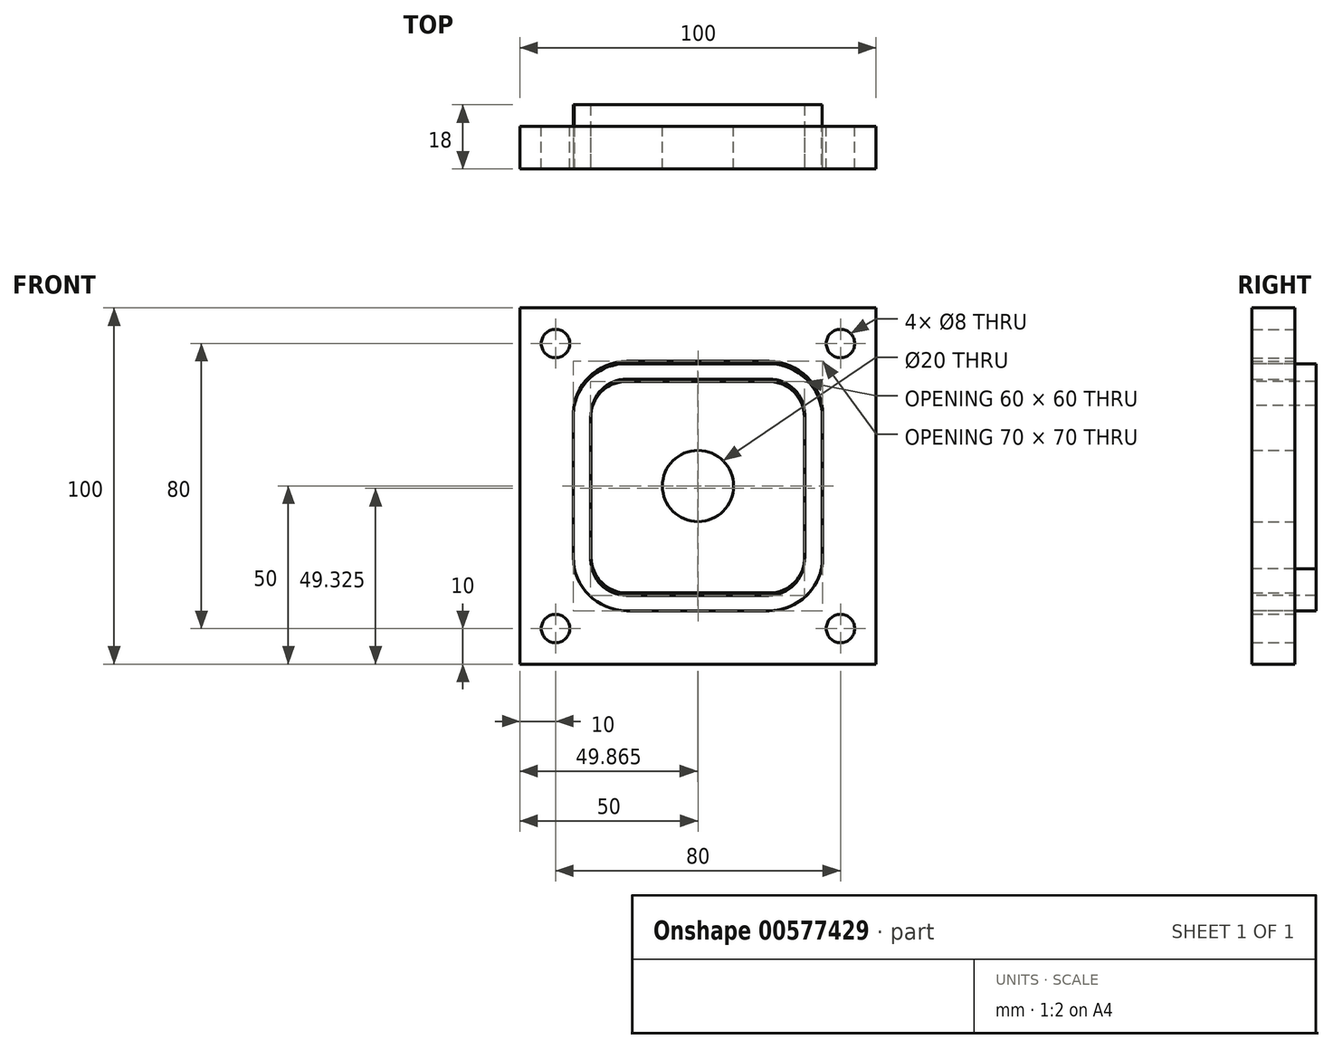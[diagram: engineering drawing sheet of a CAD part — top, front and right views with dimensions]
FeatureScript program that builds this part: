
annotation { "Feature Type Name" : "Feature", "Feature Type Description" : "" }
export const myFeature = defineFeature(function(context is Context, id is Id, definition is map)
    precondition{}
    {
        {
            var Q0;
            Q0=qCreatedBy(makeId("Front.planeOp"),FACE);
            var sketch = newSketch(context, id + "F0", { "sketchPlane" : qUnion([Q0])});
            skLineSegment(sketch, "E0", {"start": v(50, -50) * mm, "end": v(50, 50) * mm});
            skLineSegment(sketch, "E1", {"start": v(50, 50) * mm, "end": v(-50, 50) * mm});
            skLineSegment(sketch, "E2", {"start": v(-50, 50) * mm, "end": v(-50, -50) * mm});
            skLineSegment(sketch, "E3", {"start": v(-50, -50) * mm, "end": v(50, -50) * mm});
            skCircle(sketch, "E4", {"center": v(40, -40) * mm, "radius": 4 * mm});
            skCircle(sketch, "E5", {"center": v(40, 40) * mm, "radius": 4 * mm});
            skCircle(sketch, "E6", {"center": v(-40, -40) * mm, "radius": 4 * mm});
            skCircle(sketch, "E7", {"center": v(-40, 40) * mm, "radius": 4 * mm});
            skCircle(sketch, "E8", {"center": v(0, 0) * mm, "radius": 10 * mm});
            skLineSegment(sketch, "E9", {"start": v(35, -20) * mm, "end": v(35, 20) * mm});
            skLineSegment(sketch, "E10", {"start": v(20, 35) * mm, "end": v(-20, 35) * mm});
            skLineSegment(sketch, "E11", {"start": v(-35, 20) * mm, "end": v(-35, -20) * mm});
            skLineSegment(sketch, "E12", {"start": v(20, -35) * mm, "end": v(-20, -35) * mm});
            skArc(sketch, "E13", {"start": v(-35, -20) * mm, "mid": v(-30.6, -30.6) * mm, "end": v(-20, -35) * mm});
            skArc(sketch, "E14", {"start": v(20, -35) * mm, "mid": v(30.6, -30.6) * mm, "end": v(35, -20) * mm});
            skArc(sketch, "E15", {"start": v(35, 20) * mm, "mid": v(30.6, 30.6) * mm, "end": v(20, 35) * mm});
            skArc(sketch, "E16", {"start": v(-20, 35) * mm, "mid": v(-30.6, 30.6) * mm, "end": v(-35, 20) * mm});
            skLineSegment(sketch, "E17", {"start": v(20, -30) * mm, "end": v(-20, -30) * mm});
            skLineSegment(sketch, "E18", {"start": v(-30, -20) * mm, "end": v(-30, 20) * mm});
            skLineSegment(sketch, "E19", {"start": v(-20, 30) * mm, "end": v(20, 30) * mm});
            skLineSegment(sketch, "E20", {"start": v(30, -20) * mm, "end": v(30, 20) * mm});
            skArc(sketch, "E21", {"start": v(20, -30) * mm, "mid": v(27.07, -27.07) * mm, "end": v(30, -20) * mm});
            skArc(sketch, "E22", {"start": v(30, 20) * mm, "mid": v(27.07, 27.07) * mm, "end": v(20, 30) * mm});
            skArc(sketch, "E23", {"start": v(-20, 30) * mm, "mid": v(-27.07, 27.07) * mm, "end": v(-30, 20) * mm});
            skArc(sketch, "E24", {"start": v(-30, -20) * mm, "mid": v(-27.07, -27.07) * mm, "end": v(-20, -30) * mm});
            skSolve(sketch);
        }
        {
            var Q0;
            Q0=makeQuery(id+"F0.imprint","IMPRINT",FACE,{"disambiguationData":[TD([[makeQuery(id+"F0.imprint","IMPRINT",EDGE,{"derivedFrom":sQuery(id+"F0.wireOp",EDGE,"E8")}),-1.0]])]});
            var Q1;
            Q1=makeQuery(id+"F0.imprint","IMPRINT",FACE,{"disambiguationData":[TD([[makeQuery(id+"F0.imprint","IMPRINT",EDGE,{"derivedFrom":sQuery(id+"F0.wireOp",EDGE,"E0")}),1.0]])]});
            extrude(context, id + "F1", {"entities" : qUnion([Q0, Q1]), "depth" : 12 * mm, "offsetDistance" : 25 * mm});
        }
        {
            var Q0;
            Q0=makeQuery(id+"F1.opExtrude","CAP_FACE",FACE,{"disambiguationData":[OSD([sQuery(id+"F0.wireOp",EDGE,"E0"),sQuery(id+"F0.wireOp",EDGE,"E1"),sQuery(id+"F0.wireOp",EDGE,"E2"),sQuery(id+"F0.wireOp",EDGE,"E3"),sQuery(id+"F0.wireOp",EDGE,"E4"),sQuery(id+"F0.wireOp",EDGE,"E5"),sQuery(id+"F0.wireOp",EDGE,"E6"),sQuery(id+"F0.wireOp",EDGE,"E7"),sQuery(id+"F0.wireOp",EDGE,"E9"),sQuery(id+"F0.wireOp",EDGE,"E10"),sQuery(id+"F0.wireOp",EDGE,"E11"),sQuery(id+"F0.wireOp",EDGE,"E12"),sQuery(id+"F0.wireOp",EDGE,"E13"),sQuery(id+"F0.wireOp",EDGE,"E14"),sQuery(id+"F0.wireOp",EDGE,"E15"),sQuery(id+"F0.wireOp",EDGE,"E16")])],"isStart":false});
            var sketch = newSketch(context, id + "F2", { "sketchPlane" : qUnion([Q0])});
            skLineSegment(sketch, "E25", {"start": v(49.87, -50.67) * mm, "end": v(49.87, 49.33) * mm});
            skLineSegment(sketch, "E26", {"start": v(49.87, 49.33) * mm, "end": v(-50.13, 49.33) * mm});
            skLineSegment(sketch, "E27", {"start": v(-50.13, 49.33) * mm, "end": v(-50.13, -50.67) * mm});
            skLineSegment(sketch, "E28", {"start": v(-50.13, -50.67) * mm, "end": v(49.87, -50.67) * mm});
            skCircle(sketch, "E29", {"center": v(39.87, -40.67) * mm, "radius": 4 * mm});
            skCircle(sketch, "E30", {"center": v(39.87, 39.33) * mm, "radius": 4 * mm});
            skCircle(sketch, "E31", {"center": v(-40.13, -40.67) * mm, "radius": 4 * mm});
            skCircle(sketch, "E32", {"center": v(-40.13, 39.33) * mm, "radius": 4 * mm});
            skCircle(sketch, "E33", {"center": v(-0.13, -0.67) * mm, "radius": 10 * mm});
            skLineSegment(sketch, "E34", {"start": v(34.87, -20.67) * mm, "end": v(34.87, 19.33) * mm});
            skLineSegment(sketch, "E35", {"start": v(19.87, 34.33) * mm, "end": v(-20.13, 34.33) * mm});
            skLineSegment(sketch, "E36", {"start": v(-35.13, 19.33) * mm, "end": v(-35.13, -20.67) * mm});
            skLineSegment(sketch, "E37", {"start": v(19.87, -35.67) * mm, "end": v(-20.13, -35.67) * mm});
            skArc(sketch, "E38", {"start": v(-35.13, -20.67) * mm, "mid": v(-30.74, -31.28) * mm, "end": v(-20.13, -35.67) * mm});
            skArc(sketch, "E39", {"start": v(19.87, -35.67) * mm, "mid": v(30.47, -31.28) * mm, "end": v(34.87, -20.67) * mm});
            skArc(sketch, "E40", {"start": v(34.87, 19.33) * mm, "mid": v(30.47, 29.93) * mm, "end": v(19.87, 34.33) * mm});
            skArc(sketch, "E41", {"start": v(-20.13, 34.33) * mm, "mid": v(-30.74, 29.93) * mm, "end": v(-35.13, 19.33) * mm});
            skLineSegment(sketch, "E42", {"start": v(19.87, -30.67) * mm, "end": v(-20.13, -30.67) * mm});
            skLineSegment(sketch, "E43", {"start": v(-30.13, -20.67) * mm, "end": v(-30.13, 19.33) * mm});
            skLineSegment(sketch, "E44", {"start": v(-20.13, 29.33) * mm, "end": v(19.87, 29.33) * mm});
            skLineSegment(sketch, "E45", {"start": v(29.87, -20.67) * mm, "end": v(29.87, 19.33) * mm});
            skArc(sketch, "E46", {"start": v(19.87, -30.67) * mm, "mid": v(26.94, -27.75) * mm, "end": v(29.87, -20.67) * mm});
            skArc(sketch, "E47", {"start": v(29.87, 19.33) * mm, "mid": v(26.94, 26.4) * mm, "end": v(19.87, 29.33) * mm});
            skArc(sketch, "E48", {"start": v(-20.13, 29.33) * mm, "mid": v(-27.2, 26.4) * mm, "end": v(-30.13, 19.33) * mm});
            skArc(sketch, "E49", {"start": v(-30.13, -20.67) * mm, "mid": v(-27.2, -27.75) * mm, "end": v(-20.13, -30.67) * mm});
            skSolve(sketch);
        }
        {
            var Q0;
            {var subQ9=sQuery(id+"F2.wireOp",EDGE,"E34");Q0=makeQuery(id+"F2.imprint","IMPRINT",FACE,{"disambiguationData":[TD([[makeQuery(id+"F2.imprint","IMPRINT",EDGE,{"derivedFrom":subQ9}),1.0]])]});}
            extrude(context, id + "F3", {"entities" : qUnion([Q0]), "oppositeDirection" : true, "depth" : 18 * mm, "offsetDistance" : 25 * mm});
        }
    });
